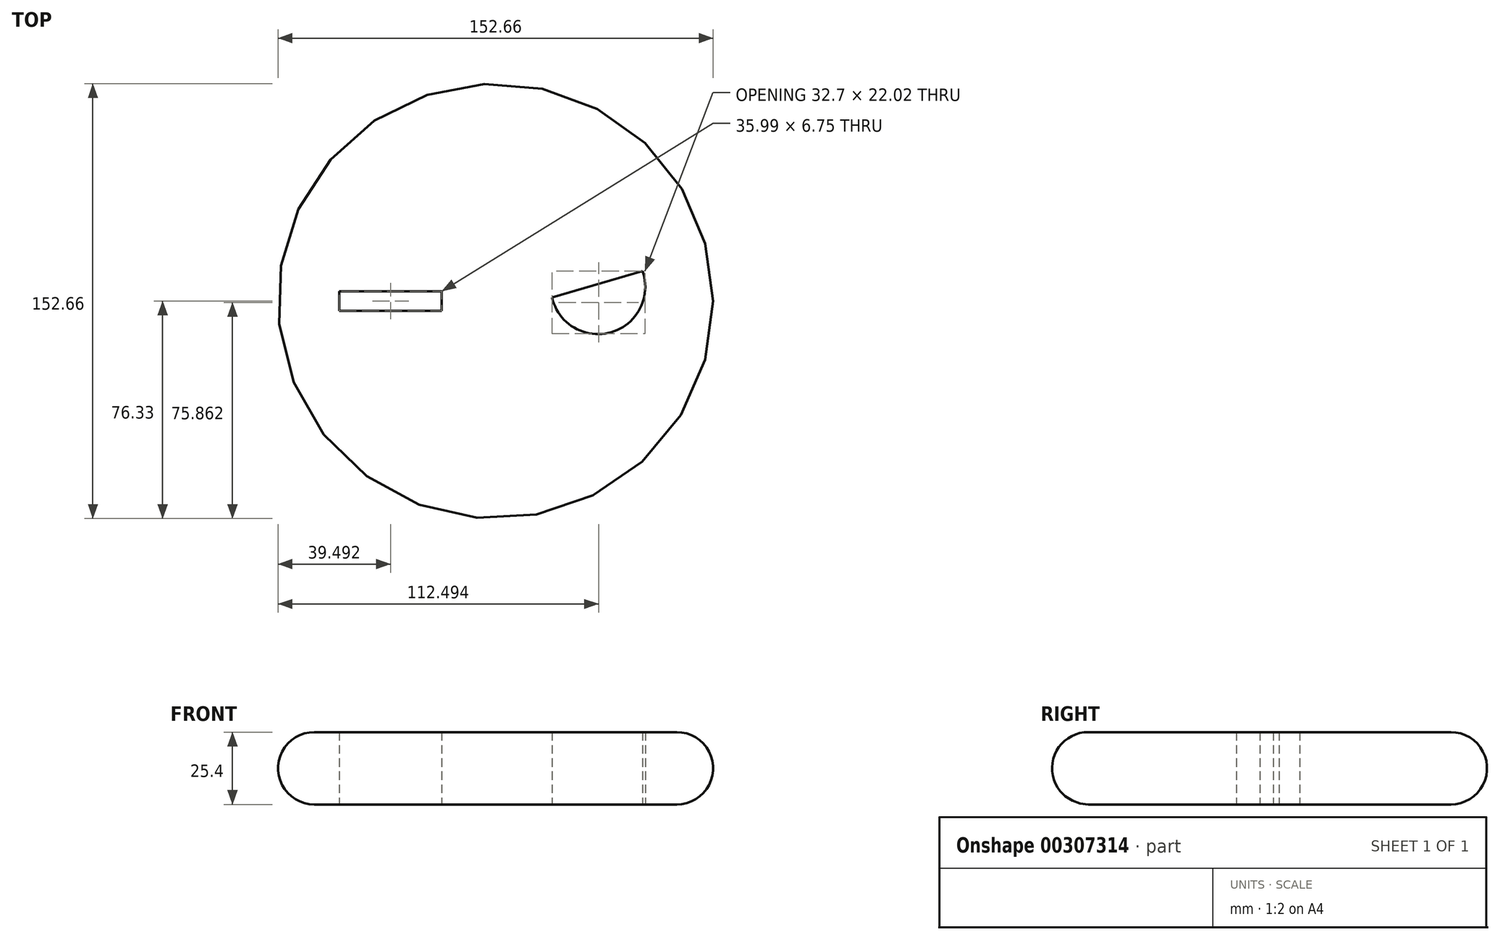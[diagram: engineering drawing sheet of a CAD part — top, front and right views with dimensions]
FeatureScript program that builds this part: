
annotation { "Feature Type Name" : "Feature", "Feature Type Description" : "" }
export const myFeature = defineFeature(function(context is Context, id is Id, definition is map)
    precondition{}
    {
        {
            var Q0;
            Q0=qCreatedBy(makeId("Top.planeOp"),FACE);
            var sketch = newSketch(context, id + "F0", { "sketchPlane" : qUnion([Q0])});
            skCircle(sketch, "E0", {"center": v(0, 0) * mm, "radius": 76.33 * mm});
            skCircle(sketch, "E1", {"center": v(0, 0) * mm, "radius": 71.72 * mm});
            skLineSegment(sketch, "E2", {"start": v(0, 71.72) * mm, "end": v(0, -73.83) * mm});
            skLineSegment(sketch, "E3", {"start": v(-54.84, -3.37) * mm, "end": v(-18.84, -3.37) * mm});
            skLineSegment(sketch, "E4.MirrorCS", {"start": v(-54.84, 3.37) * mm, "end": v(-18.84, 3.37) * mm});
            skLineSegment(sketch, "E5", {"start": v(-54.84, 3.37) * mm, "end": v(-54.84, -3.37) * mm});
            skLineSegment(sketch, "E6", {"start": v(-18.84, 3.37) * mm, "end": v(-18.84, -3.37) * mm});
            skLineSegment(sketch, "E7", {"start": v(19.81, 1.26) * mm, "end": v(51.59, 10.54) * mm});
            skArc(sketch, "E8", {"start": v(19.81, 1.26) * mm, "mid": v(40.62, -10.94) * mm, "end": v(51.59, 10.54) * mm});
            skSolve(sketch);
        }
        {
            var Q0;
            Q0=makeQuery(id+"F0.imprint","IMPRINT",FACE,{"disambiguationData":[TD([[makeQuery(id+"F0.imprint","IMPRINT",EDGE,{"derivedFrom":sQuery(id+"F0.wireOp",EDGE,"E7")}),1.0]])]});
            var Q1;
            Q1=makeQuery(id+"F0.imprint","IMPRINT",FACE,{"disambiguationData":[TD([[makeQuery(id+"F0.imprint","IMPRINT",EDGE,{"derivedFrom":sQuery(id+"F0.wireOp",EDGE,"E3")}),-1.0]])]});
            var Q2;
            Q2=makeQuery(id+"F0.imprint","IMPRINT",FACE,{"disambiguationData":[TD([[makeQuery(id+"F0.imprint","IMPRINT",EDGE,{"derivedFrom":sQuery(id+"F0.wireOp",EDGE,"E0")}),1.0]])]});
            extrude(context, id + "F1", {"entities" : qUnion([Q0, Q1, Q2]), "depth" : 25.4 * mm});
        }
        {
            var Q0;
            Q0=makeQuery(id+"F1.opExtrude","CAP_EDGE",EDGE,{"disambiguationData":[OSD([sQuery(id+"F0.wireOp",EDGE,"E0")])],"isStart":false});
            var Q1;
            Q1=makeQuery(id+"F1.opExtrude","CAP_EDGE",EDGE,{"disambiguationData":[OSD([sQuery(id+"F0.wireOp",EDGE,"E0")])],"isStart":true});
            fillet(context, id + "F2", {"entities" : qUnion([Q0, Q1]), "radius" : 12.7 * mm, "tangentPropagation" : true, "allowEdgeOverflow" : false});
        }
    });
